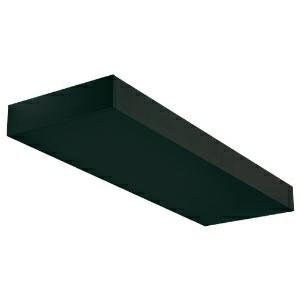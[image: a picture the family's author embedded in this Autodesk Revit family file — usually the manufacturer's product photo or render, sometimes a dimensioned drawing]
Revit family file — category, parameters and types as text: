
# Revit family: speed_wall_uplight_310-4200
name_source: partatom
category: Lighting Fixtures
units: mm (PartAtom-declared; Revit-internal decimal feet)

## family parameters
Cut with Voids When Loaded = No
Host = Face
Light Source = No
Part Type = Normal
Room Calculation Point = No
Round Connector Dimension = Use Diameter
Shared = No

## types (1)
- 310-4200-F01-S27 (2 x LED, 1310 lm, 8.6 W, 2700K)
    Apparent Load = 17 VA
    CIE Flux Codes = 0 0 0 0 83
    Color Rendering = 1B/80…89
    Color Temperature = 2700K
    Default Elevation = 1800 mm
    Description = SPEED WALL UPLIGHT
    Height = 50 mm
    Lamp = 2 x LED
    Lamp Light Flux = 1310 lm
    Lamp Power = 8.6 W
    Lamp count = 2
    Length = 320 mm
    Luminous efficacy = 127 lm/W
    Manufacturer = Prolicht
    ModVariant = No
    Model = 310-4200
    Mounting Place = Ceiling
    Mounting Type = Surface mounted
    Number of Poles = 1
    OnlyDefault = Yes
    Power Factor = 1
    Product Name = SPEED WALL UPLIGHT
    Product group = Surface lights
    ProductGroupID = 331
    Protection Class = Protection class
    Protection Degree = Degree of protection
    RLX_Detail_Level = 1
    RLX_Emergency_Light_Flux = 0 lm
    RLX_Emergency_Type = 0
    RLX_Emergency_Type_DB = No
    RlxData = <blob elided: 70013 chars, md5=cfb845b1>
    Socket = socket
    Standby Power = 0 W
    System Light Flux = 2185 lm
    System Power = 17 W
    Type Comments = DIFFUSER INDIRECT Opal (01),LED COLOUR IND 2700 K (27)
    Type Image = 310-4200.jpg
    URL = http://relux.com
    VarID = 310-4200-f01-s27
    Voltage = 0 V
    Weight = 0.00 kg
    Width = 195 mm

## geometry (parser evidence)
native form markers: Blend x4, Sweep x11
no freeform markers — native parametric forms only
